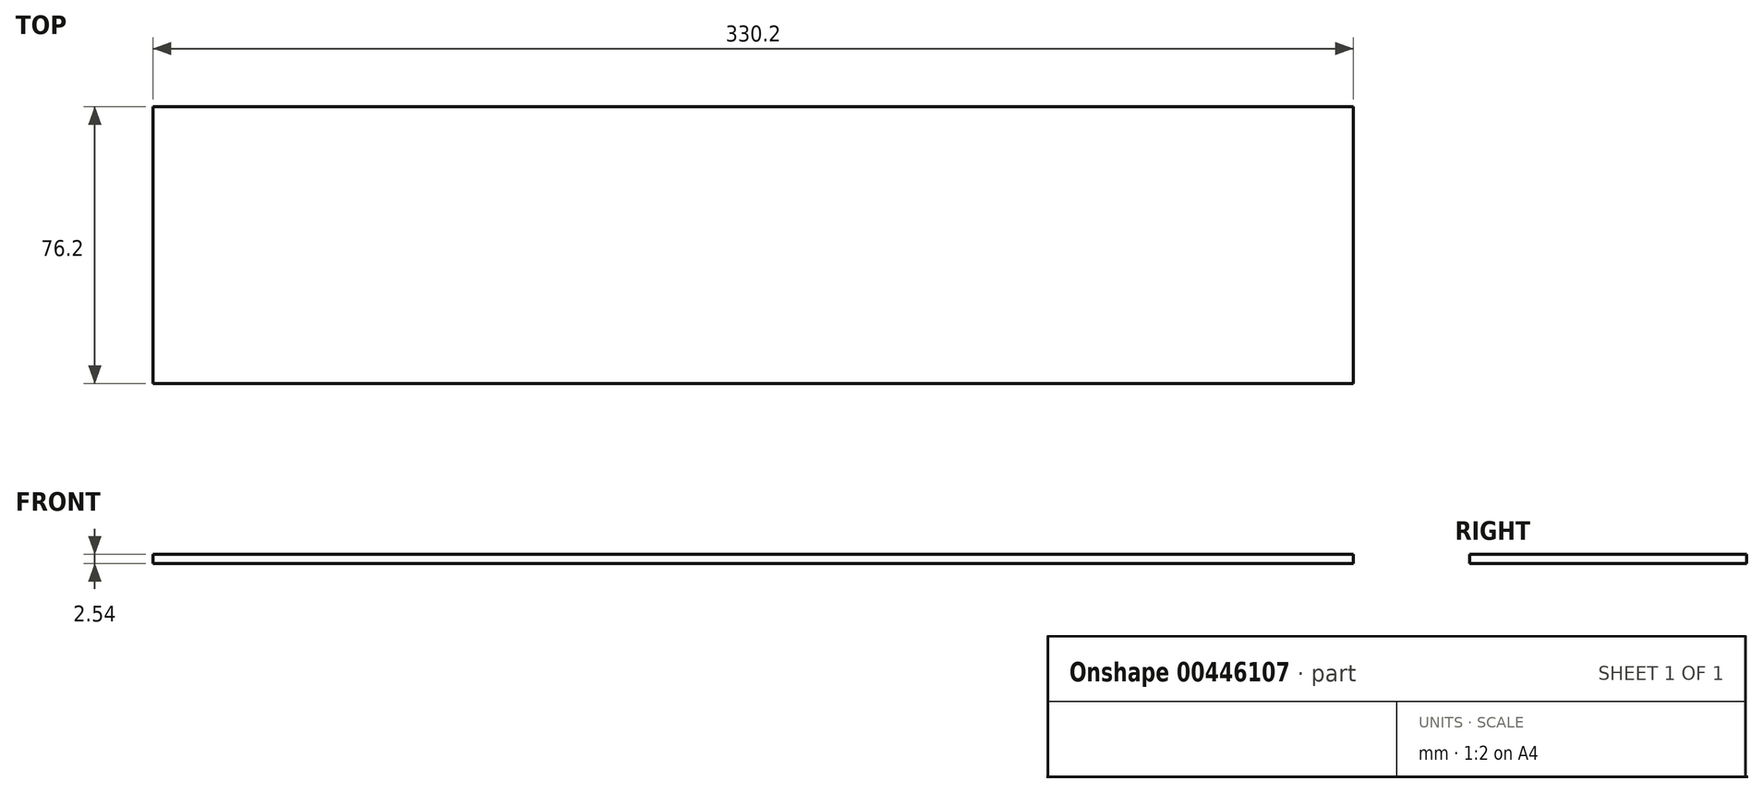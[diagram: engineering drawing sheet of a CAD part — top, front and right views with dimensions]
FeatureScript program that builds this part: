
annotation { "Feature Type Name" : "Feature", "Feature Type Description" : "" }
export const myFeature = defineFeature(function(context is Context, id is Id, definition is map)
    precondition{}
    {
        {
            var Q0;
            Q0=qCreatedBy(makeId("Top.planeOp"),FACE);
            var sketch = newSketch(context, id + "F0", { "sketchPlane" : qUnion([Q0])});
            skLineSegment(sketch, "E0.bottom", {"start": v(0, 0) * mm, "end": v(330.2, 0) * mm});
            skLineSegment(sketch, "E0.top", {"start": v(0, 76.2) * mm, "end": v(330.2, 76.2) * mm});
            skLineSegment(sketch, "E0.left", {"start": v(0, 0) * mm, "end": v(0, 76.2) * mm});
            skLineSegment(sketch, "E0.right", {"start": v(330.2, 0) * mm, "end": v(330.2, 76.2) * mm});
            skSolve(sketch);
        }
        {
            var Q0;
            Q0=makeQuery(id+"F0.imprint","IMPRINT",FACE,{"disambiguationData":[TD([[makeQuery(id+"F0.imprint","IMPRINT",EDGE,{"derivedFrom":sQuery(id+"F0.wireOp",EDGE,"E0.bottom")}),1.0]])]});
            extrude(context, id + "F1", {"entities" : qUnion([Q0]), "depth" : 2.54 * mm});
        }
    });
